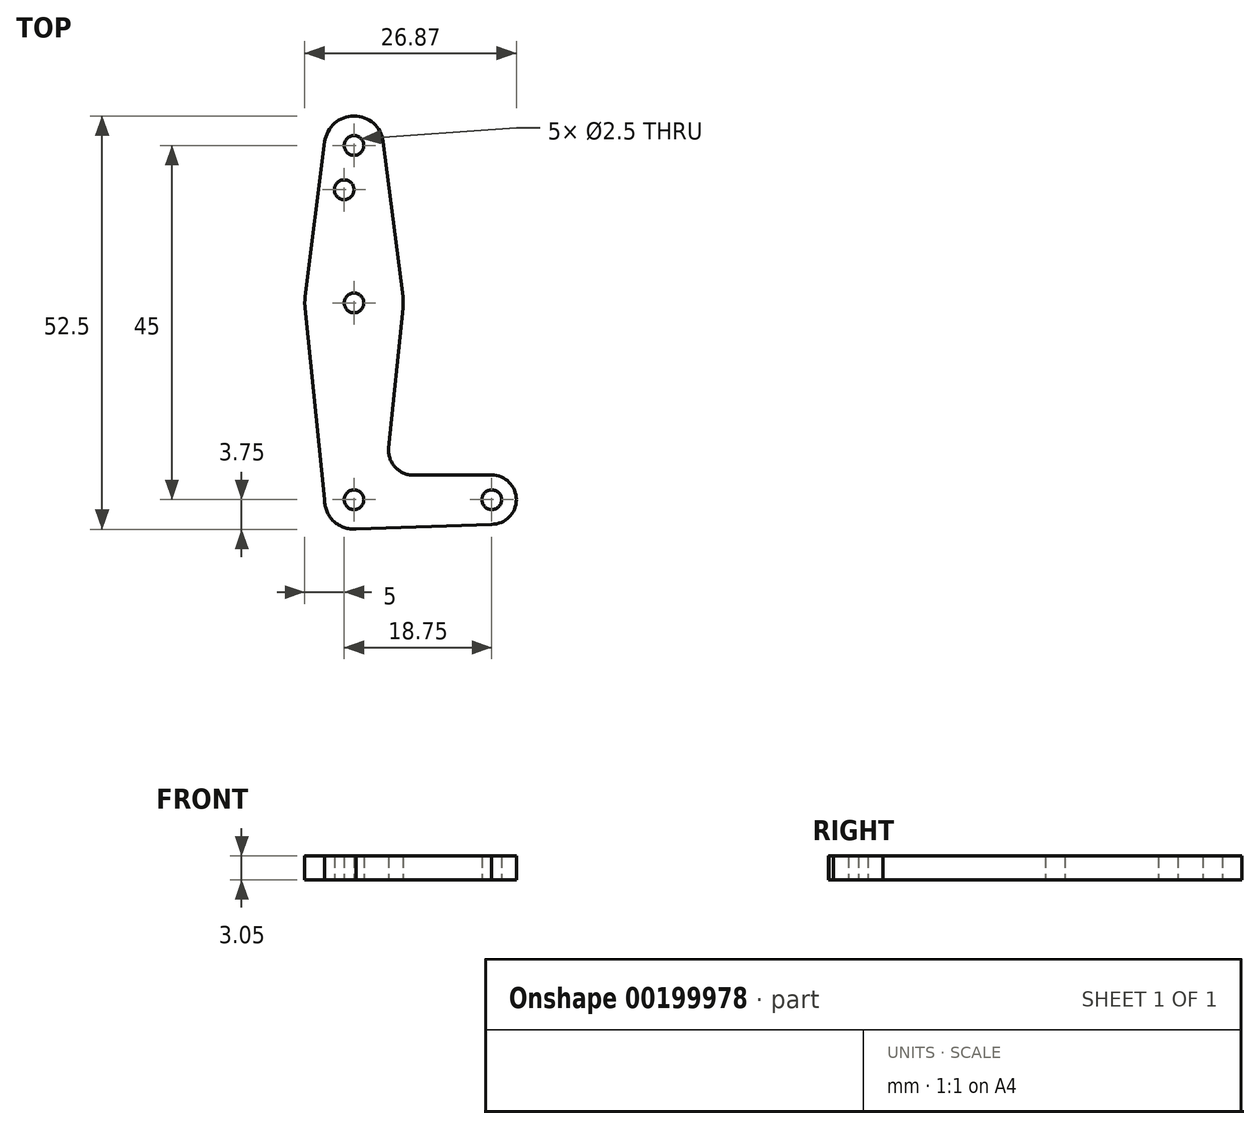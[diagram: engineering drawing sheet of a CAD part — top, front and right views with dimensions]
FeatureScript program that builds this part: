
annotation { "Feature Type Name" : "Feature", "Feature Type Description" : "" }
export const myFeature = defineFeature(function(context is Context, id is Id, definition is map)
    precondition{}
    {
        {
            var Q0;
            Q0=qCreatedBy(makeId("Top.planeOp"),FACE);
            var sketch = newSketch(context, id + "F0", { "sketchPlane" : qUnion([Q0])});
            skLineSegment(sketch, "E0", {"start": v(0, 45) * mm, "end": v(0, 0) * mm, "construction": true});
            skLineSegment(sketch, "E1", {"start": v(0, 0) * mm, "end": v(17.5, 0) * mm, "construction": true});
            skCircle(sketch, "E2", {"center": v(0, 0) * mm, "radius": 3.75 * mm});
            skCircle(sketch, "E3", {"center": v(0, 25) * mm, "radius": 6.25 * mm});
            skCircle(sketch, "E4", {"center": v(0, 45) * mm, "radius": 3.75 * mm});
            skCircle(sketch, "E5", {"center": v(17.5, 0) * mm, "radius": 3.12 * mm});
            skLineSegment(sketch, "E6", {"start": v(-3.75, 0) * mm, "end": v(-6.22, 24.37) * mm});
            skLineSegment(sketch, "E7", {"start": v(7.53, 3.12) * mm, "end": v(17.5, 3.12) * mm});
            skLineSegment(sketch, "E8", {"start": v(0, -3.75) * mm, "end": v(17.5, -3.13) * mm});
            skLineSegment(sketch, "E9", {"start": v(-3.72, 45.47) * mm, "end": v(-6.2, 25.78) * mm});
            skLineSegment(sketch, "E10", {"start": v(3.72, 45.47) * mm, "end": v(6.2, 25.78) * mm});
            skLineSegment(sketch, "E11", {"start": v(6.22, 24.37) * mm, "end": v(4.42, 6.57) * mm});
            skCircle(sketch, "E12", {"center": v(0, 45) * mm, "radius": 1.25 * mm});
            skCircle(sketch, "E13", {"center": v(0, 25) * mm, "radius": 1.25 * mm});
            skCircle(sketch, "E14", {"center": v(0, 0) * mm, "radius": 1.25 * mm});
            skCircle(sketch, "E15", {"center": v(17.5, 0) * mm, "radius": 1.25 * mm});
            skCircle(sketch, "E16", {"center": v(-1.25, 39.38) * mm, "radius": 1.25 * mm});
            skPoint(sketch, "E17.newPointA", {"position": v(3.75, 0) * mm});
            skArc(sketch, "E17.filletArc", {"start": v(4.42, 6.57) * mm, "mid": v(5.2, 4.16) * mm, "end": v(7.53, 3.12) * mm});
            skSolve(sketch);
        }
        {
            var Q0;
            Q0 = qSketchRegion(id + "F0", true);
            extrude(context, id + "F1", {"entities" : qUnion([Q0]), "depth" : 3.05 * mm});
        }
    });
